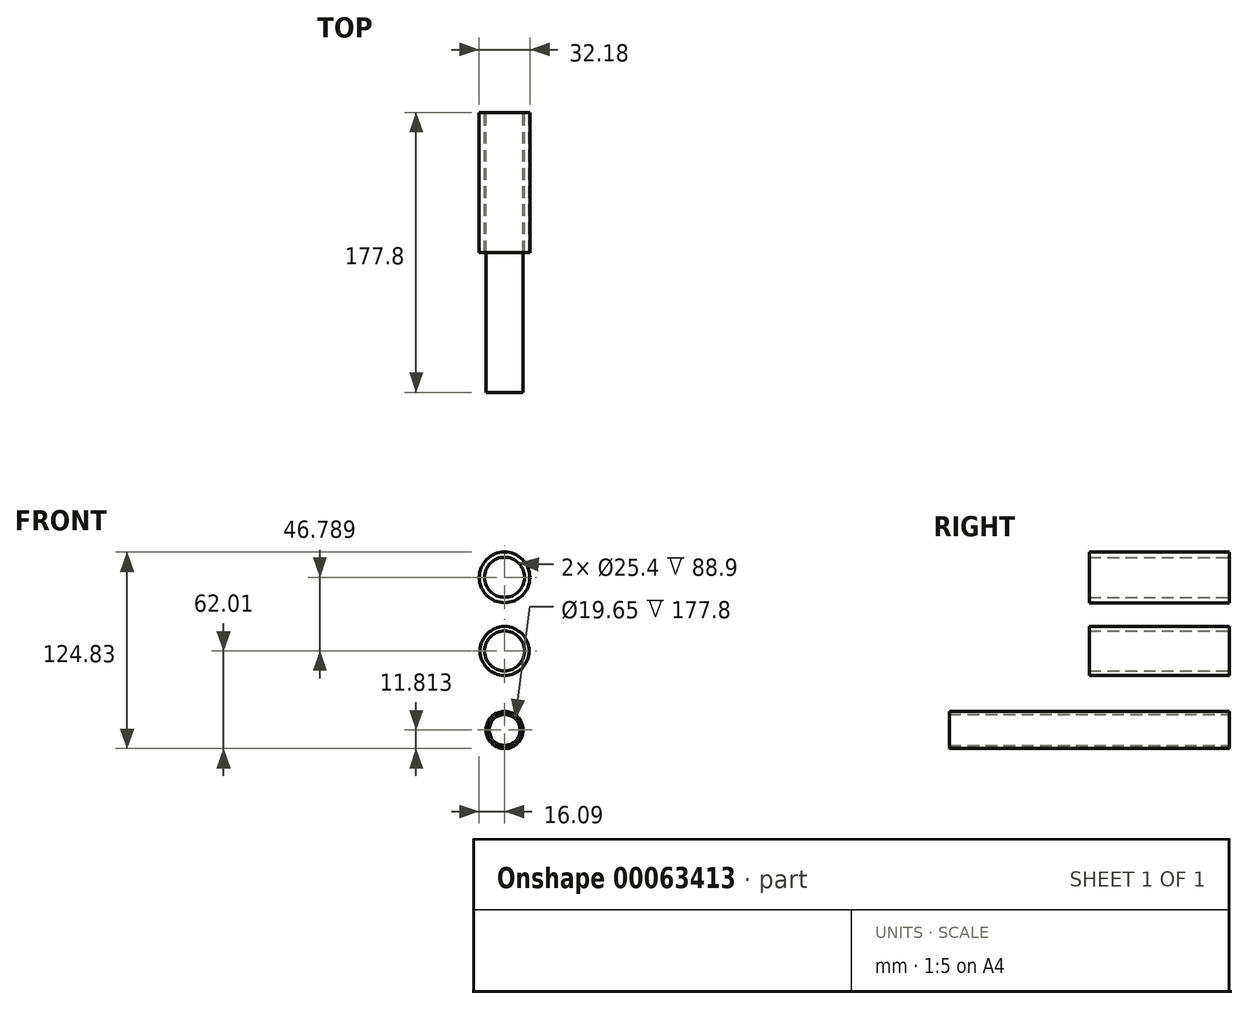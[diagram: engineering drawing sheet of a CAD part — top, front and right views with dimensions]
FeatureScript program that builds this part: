
annotation { "Feature Type Name" : "Feature", "Feature Type Description" : "" }
export const myFeature = defineFeature(function(context is Context, id is Id, definition is map)
    precondition{}
    {
        {
            var Q0;
            Q0=qCreatedBy(makeId("Front.planeOp"),FACE);
            var sketch = newSketch(context, id + "F0", { "sketchPlane" : qUnion([Q0])});
            skCircle(sketch, "E0", {"center": v(0, 0) * mm, "radius": 15.5 * mm});
            skCircle(sketch, "E1", {"center": v(0, 0) * mm, "radius": 12.7 * mm});
            skSolve(sketch);
        }
        {
            var Q0;
            Q0=makeQuery(id+"F0.imprint","IMPRINT",FACE,{"disambiguationData":[TD([[makeQuery(id+"F0.imprint","IMPRINT",EDGE,{"derivedFrom":sQuery(id+"F0.wireOp",EDGE,"E0")}),1.0]])]});
            extrude(context, id + "F1", {"entities" : qUnion([Q0]), "depth" : 88.9 * mm});
        }
        {
            var Q0;
            Q0=qCreatedBy(makeId("Front.planeOp"),FACE);
            var sketch = newSketch(context, id + "F2", { "sketchPlane" : qUnion([Q0])});
            skCircle(sketch, "E2", {"center": v(0, 46.79) * mm, "radius": 12.7 * mm});
            skCircle(sketch, "E3", {"center": v(0, 46.73) * mm, "radius": 16.09 * mm});
            skSolve(sketch);
        }
        {
            var Q0;
            Q0 = qSketchRegion(id + "F2", true);
            extrude(context, id + "F3", {"entities" : qUnion([Q0]), "depth" : 88.9 * mm});
        }
        {
            var Q0;
            Q0=qCreatedBy(makeId("Front.planeOp"),FACE);
            var sketch = newSketch(context, id + "F4", { "sketchPlane" : qUnion([Q0])});
            skCircle(sketch, "E4", {"center": v(0, -50.2) * mm, "radius": 11.81 * mm});
            skCircle(sketch, "E5", {"center": v(0, -50.2) * mm, "radius": 9.83 * mm});
            skSolve(sketch);
        }
        {
            var Q0;
            Q0 = qSketchRegion(id + "F4", true);
            extrude(context, id + "F5", {"entities" : qUnion([Q0]), "depth" : 177.8 * mm});
        }
    });
